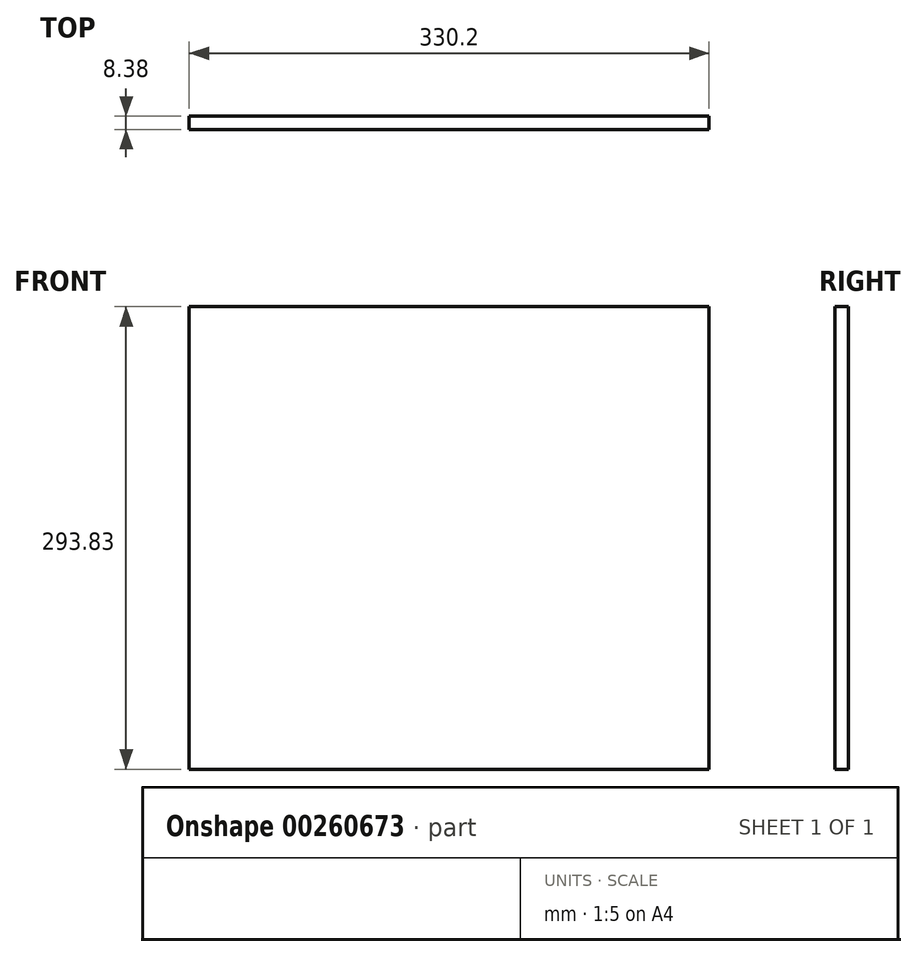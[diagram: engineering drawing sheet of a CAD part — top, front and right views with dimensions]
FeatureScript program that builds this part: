
annotation { "Feature Type Name" : "Feature", "Feature Type Description" : "" }
export const myFeature = defineFeature(function(context is Context, id is Id, definition is map)
    precondition{}
    {
        {
            var Q0;
            Q0=qCreatedBy(makeId("Front.planeOp"),FACE);
            var sketch = newSketch(context, id + "F0", { "sketchPlane" : qUnion([Q0])});
            skLineSegment(sketch, "E0.bottom", {"start": v(-162.95, 153.23) * mm, "end": v(167.25, 153.23) * mm});
            skLineSegment(sketch, "E0.top", {"start": v(-162.95, -140.6) * mm, "end": v(167.25, -140.6) * mm});
            skLineSegment(sketch, "E0.left", {"start": v(-162.95, 153.23) * mm, "end": v(-162.95, -140.6) * mm});
            skLineSegment(sketch, "E0.right", {"start": v(167.25, 153.23) * mm, "end": v(167.25, -140.6) * mm});
            skSolve(sketch);
        }
        {
            var Q0;
            Q0 = qSketchRegion(id + "F0", true);
            extrude(context, id + "F1", {"entities" : qUnion([Q0]), "depth" : 8.38 * mm});
        }
    });
